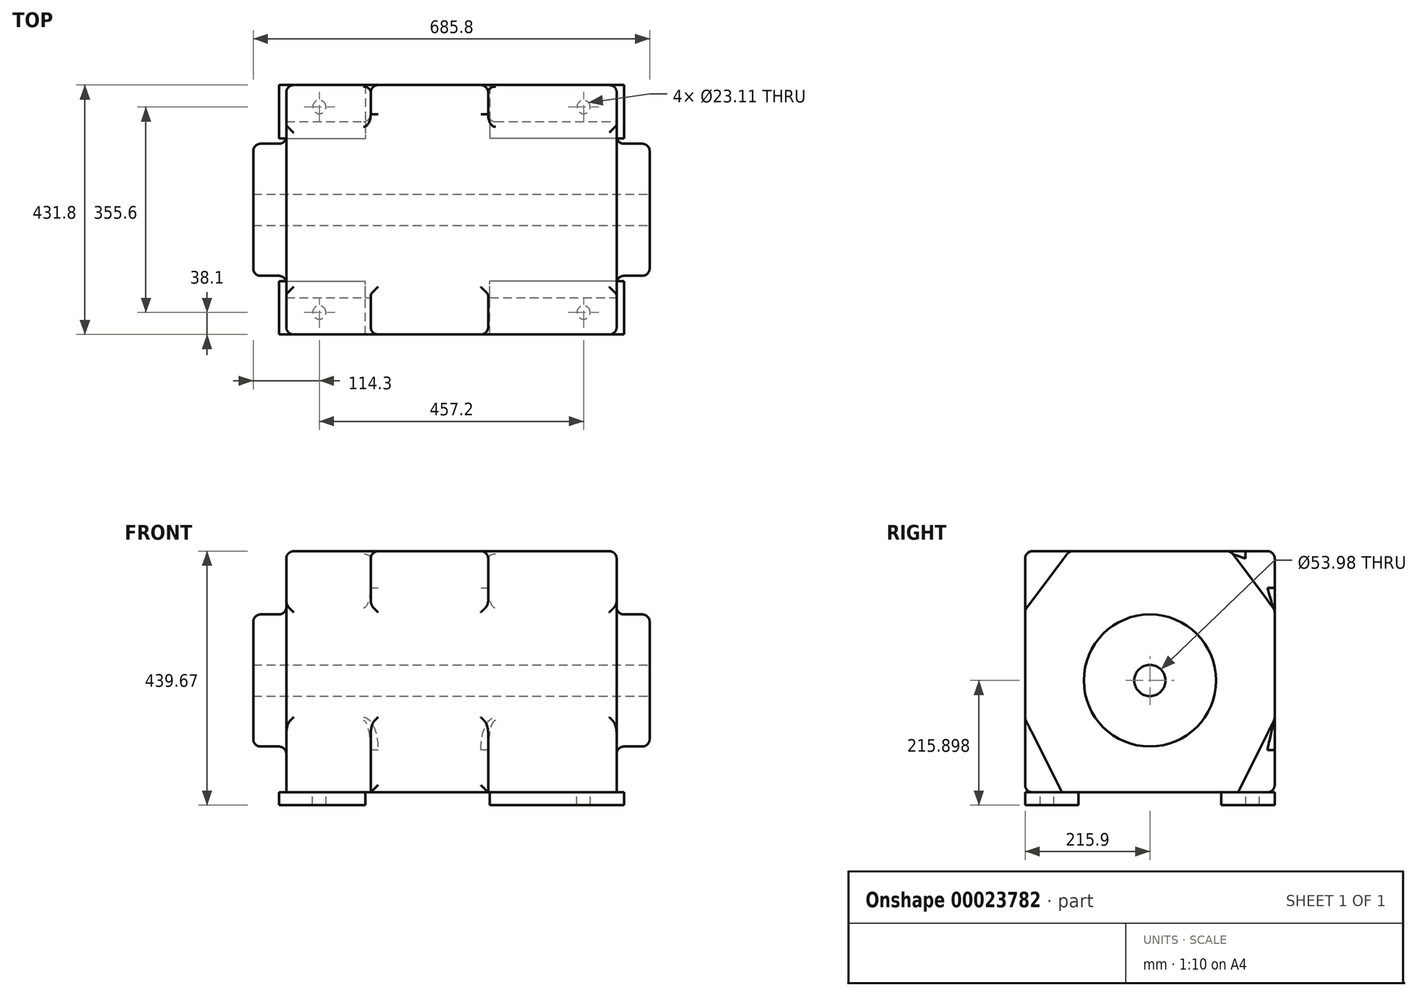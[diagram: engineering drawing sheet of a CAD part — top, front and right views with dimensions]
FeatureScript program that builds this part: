
annotation { "Feature Type Name" : "Feature", "Feature Type Description" : "" }
export const myFeature = defineFeature(function(context is Context, id is Id, definition is map)
    precondition{}
    {
        {
            var Q0;
            Q0=qCreatedBy(makeId("Top.planeOp"),FACE);
            var sketch = newSketch(context, id + "F0", { "sketchPlane" : qUnion([Q0])});
            skLineSegment(sketch, "E0", {"start": v(0, 97.33) * mm, "end": v(0, -215.9) * mm, "construction": true});
            skLineSegment(sketch, "E1", {"start": v(-109.5, 0) * mm, "end": v(101.39, 0) * mm, "construction": true});
            skLineSegment(sketch, "E2.0", {"start": v(-298.45, 215.9) * mm, "end": v(-298.45, -215.9) * mm, "construction": true});
            skLineSegment(sketch, "E3.0", {"start": v(-298.45, -215.9) * mm, "end": v(298.45, -215.9) * mm, "construction": true});
            skLineSegment(sketch, "E4.MirrorCS", {"start": v(298.45, 215.9) * mm, "end": v(298.45, -215.9) * mm, "construction": true});
            skLineSegment(sketch, "E5.MirrorCS", {"start": v(-298.45, 215.9) * mm, "end": v(298.45, 215.9) * mm, "construction": true});
            skPoint(sketch, "E6.orphan", {"position": v(-298.45, 97.33) * mm});
            skPoint(sketch, "E7.orphan", {"position": v(298.45, 97.33) * mm});
            skLineSegment(sketch, "E8.bottom", {"start": v(-298.45, -215.9) * mm, "end": v(-149.1, -215.9) * mm});
            skLineSegment(sketch, "E8.top", {"start": v(-298.45, -123.7) * mm, "end": v(-149.1, -123.7) * mm});
            skLineSegment(sketch, "E8.left", {"start": v(-298.45, -215.9) * mm, "end": v(-298.45, -123.7) * mm});
            skLineSegment(sketch, "E8.right", {"start": v(-149.1, -215.9) * mm, "end": v(-149.1, -123.7) * mm});
            skLineSegment(sketch, "E9.bottom", {"start": v(298.45, -215.9) * mm, "end": v(66.55, -215.9) * mm});
            skLineSegment(sketch, "E9.top", {"start": v(298.45, -123.7) * mm, "end": v(66.55, -123.7) * mm});
            skLineSegment(sketch, "E9.left", {"start": v(298.45, -215.9) * mm, "end": v(298.45, -123.7) * mm});
            skLineSegment(sketch, "E9.right", {"start": v(66.55, -215.9) * mm, "end": v(66.55, -123.7) * mm});
            skLineSegment(sketch, "E10.0", {"start": v(-228.6, 97.33) * mm, "end": v(-228.6, -215.9) * mm, "construction": true});
            skLineSegment(sketch, "E11.0", {"start": v(-228.6, -177.8) * mm, "end": v(101.39, -177.8) * mm, "construction": true});
            skCircle(sketch, "E12", {"center": v(-228.6, -177.8) * mm, "radius": 11.56 * mm});
            skCircle(sketch, "E13.MirrorC", {"center": v(228.6, -177.8) * mm, "radius": 11.56 * mm});
            skCircle(sketch, "E14.MirrorC", {"center": v(-228.6, 177.8) * mm, "radius": 11.56 * mm});
            skLineSegment(sketch, "E15.MirrorCS", {"start": v(-298.45, 123.7) * mm, "end": v(-149.1, 123.7) * mm});
            skLineSegment(sketch, "E16.MirrorCS", {"start": v(-298.45, 215.9) * mm, "end": v(-149.1, 215.9) * mm});
            skLineSegment(sketch, "E17.MirrorCS", {"start": v(-298.45, 215.9) * mm, "end": v(-298.45, 123.7) * mm});
            skLineSegment(sketch, "E18.MirrorCS", {"start": v(-149.1, 215.9) * mm, "end": v(-149.1, 123.7) * mm});
            skLineSegment(sketch, "E19.MirrorCS", {"start": v(298.45, 215.9) * mm, "end": v(298.45, 123.7) * mm});
            skLineSegment(sketch, "E20.MirrorCS", {"start": v(-228.6, 177.8) * mm, "end": v(101.39, 177.8) * mm, "construction": true});
            skLineSegment(sketch, "E21.MirrorCS", {"start": v(-298.45, 215.9) * mm, "end": v(298.45, 215.9) * mm});
            skLineSegment(sketch, "E22.MirrorCS", {"start": v(298.45, 123.7) * mm, "end": v(66.55, 123.7) * mm});
            skCircle(sketch, "E23.MirrorC", {"center": v(228.6, 177.8) * mm, "radius": 11.56 * mm});
            skLineSegment(sketch, "E24.MirrorCS", {"start": v(298.45, 215.9) * mm, "end": v(66.55, 215.9) * mm});
            skLineSegment(sketch, "E25.MirrorCS", {"start": v(66.55, 215.9) * mm, "end": v(66.55, 123.7) * mm});
            skSolve(sketch);
        }
        {
            var Q0;
            Q0 = qSketchRegion(id + "F0", true);
            extrude(context, id + "F1", {"entities" : qUnion([Q0]), "oppositeDirection" : true, "depth" : 22.35 * mm});
        }
        {
            var Q0;
            Q0=makeQuery(id+"F1.opExtrude","CAP_FACE",FACE,{"disambiguationData":[OSD([sQuery(id+"F0.wireOp",EDGE,"E14.MirrorC"),sQuery(id+"F0.wireOp",EDGE,"E15.MirrorCS"),sQuery(id+"F0.wireOp",EDGE,"E17.MirrorCS"),sQuery(id+"F0.wireOp",EDGE,"E18.MirrorCS"),sQuery(id+"F0.wireOp",EDGE,"E21.MirrorCS")])],"isStart":true});
            var sketch = newSketch(context, id + "F2", { "sketchPlane" : qUnion([Q0])});
            skLineSegment(sketch, "E26.bottom", {"start": v(-285.75, 139.7) * mm, "end": v(285.75, 139.7) * mm});
            skLineSegment(sketch, "E26.top", {"start": v(-285.75, -139.7) * mm, "end": v(285.75, -139.7) * mm});
            skLineSegment(sketch, "E26.left", {"start": v(-285.75, 139.7) * mm, "end": v(-285.75, -139.7) * mm});
            skLineSegment(sketch, "E26.right", {"start": v(285.75, 139.7) * mm, "end": v(285.75, -139.7) * mm});
            skSolve(sketch);
        }
        {
            var Q0;
            Q0 = qSketchRegion(id + "F2", true);
            extrude(context, id + "F3", {"entities" : qUnion([Q0]), "operationType" : NewBodyOperationType.ADD, "depth" : 417.32 * mm});
        }
        {
            var Q0;
            Q0=makeQuery(id+"F3.opExtrude","SWEPT_FACE",FACE,{"disambiguationData":[OSD([sQuery(id+"F2.wireOp",EDGE,"E26.right")])]});
            var sketch = newSketch(context, id + "F4", { "sketchPlane" : qUnion([Q0])});
            skLineSegment(sketch, "E27.0", {"start": v(-215.9, 0) * mm, "end": v(-123.7, 0) * mm, "construction": true});
            skLineSegment(sketch, "E28.0", {"start": v(215.9, 0) * mm, "end": v(123.7, 0) * mm, "construction": true});
            skLineSegment(sketch, "E29.0", {"start": v(139.7, 417.32) * mm, "end": v(-139.7, 417.32) * mm, "construction": true});
            skLineSegment(sketch, "E30", {"start": v(215.9, 0) * mm, "end": v(215.9, 417.32) * mm, "construction": true});
            skLineSegment(sketch, "E31.bottom", {"start": v(0, 0) * mm, "end": v(215.9, 0) * mm});
            skLineSegment(sketch, "E31.top", {"start": v(0, 417.32) * mm, "end": v(139.7, 417.32) * mm});
            skLineSegment(sketch, "E31.left", {"start": v(0, 0) * mm, "end": v(0, 417.32) * mm});
            skLineSegment(sketch, "E31.right", {"start": v(215.9, 127) * mm, "end": v(215.9, 315.72) * mm});
            skLineSegment(sketch, "E32", {"start": v(152.4, 0) * mm, "end": v(215.9, 127) * mm});
            skLineSegment(sketch, "E33", {"start": v(139.7, 417.32) * mm, "end": v(215.9, 315.72) * mm});
            skLineSegment(sketch, "E34.MirrorCS", {"start": v(-215.9, 0) * mm, "end": v(-123.7, 0) * mm});
            skLineSegment(sketch, "E35.MirrorCS", {"start": v(-152.4, 0) * mm, "end": v(-215.9, 127) * mm});
            skLineSegment(sketch, "E36.MirrorCS", {"start": v(0, 417.32) * mm, "end": v(-139.7, 417.32) * mm});
            skLineSegment(sketch, "E37.MirrorCS", {"start": v(0, 0) * mm, "end": v(-215.9, 0) * mm});
            skLineSegment(sketch, "E38.MirrorCS", {"start": v(-215.9, 127) * mm, "end": v(-215.9, 315.72) * mm});
            skLineSegment(sketch, "E39.MirrorCS", {"start": v(-215.9, 127) * mm, "end": v(-215.9, 417.32) * mm});
            skLineSegment(sketch, "E40.MirrorCS", {"start": v(-139.7, 417.32) * mm, "end": v(-215.9, 315.72) * mm});
            skSolve(sketch);
        }
        {
            var Q0;
            Q0 = qSketchRegion(id + "F4", true);
            var Q1;
            Q1=makeQuery(id+"F3.opExtrude","SWEPT_FACE",FACE,{"disambiguationData":[OSD([sQuery(id+"F2.wireOp",EDGE,"E26.left")])]});
            extrude(context, id + "F5", {"entities" : qUnion([Q0]), "operationType" : NewBodyOperationType.ADD, "endBound" : BoundingType.UP_TO_SURFACE, "oppositeDirection" : true, "endBoundEntityFace" : qUnion([Q1]), "depth" : 25.4 * mm});
        }
        {
            var Q0;
            Q0=qCreatedBy(makeId("Right.planeOp"),FACE);
            var sketch = newSketch(context, id + "F6", { "sketchPlane" : qUnion([Q0])});
            skLineSegment(sketch, "E41.0", {"start": v(-215.9, 0) * mm, "end": v(-123.7, 0) * mm, "construction": true});
            skLineSegment(sketch, "E42.0", {"start": v(215.9, 0) * mm, "end": v(123.7, 0) * mm, "construction": true});
            skLineSegment(sketch, "E43.bottom", {"start": v(215.9, 0) * mm, "end": v(-215.9, 0) * mm, "construction": true});
            skLineSegment(sketch, "E43.top", {"start": v(215.9, 0) * mm, "end": v(-215.9, 0) * mm, "construction": true});
            skLineSegment(sketch, "E43.left", {"start": v(215.9, 0) * mm, "end": v(215.9, 0) * mm});
            skLineSegment(sketch, "E43.right", {"start": v(-215.9, 0) * mm, "end": v(-215.9, 0) * mm});
            skLineSegment(sketch, "E44.0", {"start": v(139.7, 417.32) * mm, "end": v(-139.7, 417.32) * mm, "construction": true});
            skLineSegment(sketch, "E45", {"start": v(215.9, 0) * mm, "end": v(215.9, 417.32) * mm, "construction": true});
            skLineSegment(sketch, "E46.bottom", {"start": v(215.9, 417.32) * mm, "end": v(-215.9, 417.32) * mm});
            skLineSegment(sketch, "E46.top", {"start": v(215.9, 0) * mm, "end": v(-215.9, 0) * mm});
            skLineSegment(sketch, "E46.left", {"start": v(215.9, 417.32) * mm, "end": v(215.9, 0) * mm});
            skLineSegment(sketch, "E46.right", {"start": v(-215.9, 417.32) * mm, "end": v(-215.9, 0) * mm});
            skSolve(sketch);
        }
        {
            var Q0;
            Q0=makeQuery(id+"F6.imprint","IMPRINT",FACE,{"disambiguationData":[TD([[makeQuery(id+"F6.imprint","IMPRINT",EDGE,{"derivedFrom":sQuery(id+"F6.wireOp",EDGE,"E46.bottom")}),1.0]])]});
            var sketch = newSketch(context, id + "F7", { "sketchPlane" : qUnion([Q0])});
            skSolve(sketch);
        }
        {
            var Q0;
            Q0 = qSketchRegion(id + "F7", true);
            var Q1;
            Q1=makeQuery(id+"F6.imprint","IMPRINT",FACE,{"disambiguationData":[TD([[makeQuery(id+"F6.imprint","IMPRINT",EDGE,{"derivedFrom":sQuery(id+"F6.wireOp",EDGE,"E46.bottom")}),1.0]])]});
            var Q2;
            Q2=makeQuery(id+"F1.opExtrude","SWEPT_FACE",FACE,{"disambiguationData":[OSD([sQuery(id+"F0.wireOp",EDGE,"E18.MirrorCS")])]});
            extrude(context, id + "F8", {"entities" : qUnion([Q0, Q1]), "operationType" : NewBodyOperationType.ADD, "oppositeDirection" : true, "endBoundEntityFace" : qUnion([Q2]), "depth" : 139.7 * mm, "hasSecondDirection" : true, "secondDirectionOppositeDirection" : false, "secondDirectionDepth" : 63.5 * mm});
        }
        {
            var Q0;
            Q0=makeQuery(id+"F8.boolean.opBoolean","MERGE",FACE,{"derivedFrom":[makeQuery(id+"F5.opExtrude","SWEPT_FACE",FACE,{"disambiguationData":[OSD([sQuery(id+"F4.wireOp",EDGE,"E31.right")])]}),makeQuery(id+"F8.opExtrude","SWEPT_FACE",FACE,{"disambiguationData":[OSD([sQuery(id+"F6.wireOp",EDGE,"E46.left")])]})]});
            var Q1;
            Q1=makeQuery(id+"F8.boolean.opBoolean","INTERSECT",EDGE,{"derivedFrom":[makeQuery(id+"F5.opExtrude","SWEPT_FACE",FACE,{"disambiguationData":[OSD([sQuery(id+"F4.wireOp",EDGE,"E32")])]}),makeQuery(id+"F8.opExtrude","CAP_FACE",FACE,{"disambiguationData":[OSD([sQuery(id+"F6.wireOp",EDGE,"E46.bottom"),sQuery(id+"F6.wireOp",EDGE,"E46.top"),sQuery(id+"F6.wireOp",EDGE,"E46.left"),sQuery(id+"F6.wireOp",EDGE,"E46.right")])],"isStart":true})]});
            var Q2;
            Q2=makeQuery(id+"F8.boolean.opBoolean","INTERSECT",EDGE,{"derivedFrom":[makeQuery(id+"F5.opExtrude","SWEPT_FACE",FACE,{"disambiguationData":[OSD([sQuery(id+"F4.wireOp",EDGE,"E33")])]}),makeQuery(id+"F8.opExtrude","CAP_FACE",FACE,{"disambiguationData":[OSD([sQuery(id+"F6.wireOp",EDGE,"E46.bottom"),sQuery(id+"F6.wireOp",EDGE,"E46.top"),sQuery(id+"F6.wireOp",EDGE,"E46.left"),sQuery(id+"F6.wireOp",EDGE,"E46.right")])],"isStart":true})]});
            var Q3;
            Q3=makeQuery(id+"F8.boolean.opBoolean","INTERSECT",EDGE,{"derivedFrom":[makeQuery(id+"F5.opExtrude","SWEPT_FACE",FACE,{"disambiguationData":[OSD([sQuery(id+"F4.wireOp",EDGE,"E32")])]}),makeQuery(id+"F8.opExtrude","CAP_FACE",FACE,{"disambiguationData":[OSD([sQuery(id+"F6.wireOp",EDGE,"E46.bottom"),sQuery(id+"F6.wireOp",EDGE,"E46.top"),sQuery(id+"F6.wireOp",EDGE,"E46.left"),sQuery(id+"F6.wireOp",EDGE,"E46.right")])],"isStart":false})]});
            var Q4;
            Q4=makeQuery(id+"F8.boolean.opBoolean","INTERSECT",EDGE,{"derivedFrom":[makeQuery(id+"F5.opExtrude","SWEPT_FACE",FACE,{"disambiguationData":[OSD([sQuery(id+"F4.wireOp",EDGE,"E33")])]}),makeQuery(id+"F8.opExtrude","CAP_FACE",FACE,{"disambiguationData":[OSD([sQuery(id+"F6.wireOp",EDGE,"E46.bottom"),sQuery(id+"F6.wireOp",EDGE,"E46.top"),sQuery(id+"F6.wireOp",EDGE,"E46.left"),sQuery(id+"F6.wireOp",EDGE,"E46.right")])],"isStart":false})]});
            var Q5;
            Q5=makeQuery(id+"F8.boolean.opBoolean","MERGE",FACE,{"derivedFrom":[makeQuery(id+"F5.opExtrude","SWEPT_FACE",FACE,{"disambiguationData":[OSD([sQuery(id+"F4.wireOp",EDGE,"E39.MirrorCS")])]}),makeQuery(id+"F8.opExtrude","SWEPT_FACE",FACE,{"disambiguationData":[OSD([sQuery(id+"F6.wireOp",EDGE,"E46.right")])]})]});
            fillet(context, id + "F9", {"entities" : qUnion([Q0, Q1, Q2, Q3, Q4, Q5]), "radius" : 12.7 * mm, "tangentPropagation" : true, "allowEdgeOverflow" : false});
        }
        {
            var Q0;
            Q0=makeQuery(id+"F8.boolean.opBoolean","MERGE",FACE,{"derivedFrom":[makeQuery(id+"F3.opExtrude","CAP_FACE",FACE,{"disambiguationData":[OSD([sQuery(id+"F2.wireOp",EDGE,"E26.bottom"),sQuery(id+"F2.wireOp",EDGE,"E26.top"),sQuery(id+"F2.wireOp",EDGE,"E26.left"),sQuery(id+"F2.wireOp",EDGE,"E26.right")])],"isStart":false}),makeQuery(id+"F8.opExtrude","SWEPT_FACE",FACE,{"disambiguationData":[OSD([sQuery(id+"F6.wireOp",EDGE,"E46.bottom")])]})]});
            fillet(context, id + "F10", {"entities" : qUnion([Q0]), "radius" : 12.7 * mm, "tangentPropagation" : true, "allowEdgeOverflow" : false});
        }
        {
            var Q0;
            Q0=makeQuery(id+"F7.imprint","IMPRINT",FACE,{"disambiguationData":[TD([[makeQuery(id+"F7.imprint","IMPRINT",EDGE,{"derivedFrom":makeQuery(id+"F6.imprint","IMPRINT",EDGE,{"derivedFrom":sQuery(id+"F6.wireOp",EDGE,"E46.bottom")})}),1.0]])]});
            var sketch = newSketch(context, id + "F11", { "sketchPlane" : qUnion([Q0])});
            skLineSegment(sketch, "E47.0", {"start": v(-215.9, -22.35) * mm, "end": v(-123.7, -22.35) * mm, "construction": true});
            skLineSegment(sketch, "E48.0", {"start": v(-215.9, 193.55) * mm, "end": v(0, 193.55) * mm, "construction": true});
            skLineSegment(sketch, "E49", {"start": v(0, 0) * mm, "end": v(0, 468.14) * mm, "construction": true});
            skCircle(sketch, "E50", {"center": v(0, 193.55) * mm, "radius": 114.3 * mm});
            skSolve(sketch);
        }
        {
            var Q0;
            Q0 = qSketchRegion(id + "F11", true);
            extrude(context, id + "F12", {"entities" : qUnion([Q0]), "operationType" : NewBodyOperationType.ADD, "depth" : 342.9 * mm, "hasSecondDirection" : true, "secondDirectionOppositeDirection" : true, "secondDirectionDepth" : 342.9 * mm});
        }
        {
            var Q0;
            Q0=makeQuery(id+"F12.boolean.opBoolean","INTERSECT",EDGE,{"derivedFrom":[makeQuery(id+"F5.boolean.opBoolean","MERGE",FACE,{"derivedFrom":[makeQuery(id+"F3.opExtrude","SWEPT_FACE",FACE,{"disambiguationData":[OSD([sQuery(id+"F2.wireOp",EDGE,"E26.right")])]}),makeQuery(id+"F5.opExtrude","CAP_FACE",FACE,{"disambiguationData":[OSD([sQuery(id+"F4.wireOp",EDGE,"E31.bottom"),sQuery(id+"F4.wireOp",EDGE,"E31.top"),sQuery(id+"F4.wireOp",EDGE,"E31.right"),sQuery(id+"F4.wireOp",EDGE,"E32"),sQuery(id+"F4.wireOp",EDGE,"E33"),sQuery(id+"F4.wireOp",EDGE,"E35.MirrorCS"),sQuery(id+"F4.wireOp",EDGE,"E36.MirrorCS"),sQuery(id+"F4.wireOp",EDGE,"E37.MirrorCS"),sQuery(id+"F4.wireOp",EDGE,"E39.MirrorCS"),sQuery(id+"F4.wireOp",EDGE,"E40.MirrorCS")])],"isStart":true})]}),makeQuery(id+"F12.opExtrude","SWEPT_FACE",FACE,{"disambiguationData":[OSD([sQuery(id+"F11.wireOp",EDGE,"E50")])]})]});
            var Q1;
            Q1=makeQuery(id+"F12.opExtrude","CAP_EDGE",EDGE,{"disambiguationData":[OSD([sQuery(id+"F11.wireOp",EDGE,"E50")])],"isStart":false});
            var Q2;
            Q2=makeQuery(id+"F12.opExtrude","CAP_FACE",FACE,{"disambiguationData":[OSD([sQuery(id+"F11.wireOp",EDGE,"E50")])],"isStart":true});
            var Q3;
            Q3=makeQuery(id+"F12.boolean.opBoolean","INTERSECT",EDGE,{"derivedFrom":[makeQuery(id+"F5.boolean.opBoolean","MERGE",FACE,{"derivedFrom":[makeQuery(id+"F3.opExtrude","SWEPT_FACE",FACE,{"disambiguationData":[OSD([sQuery(id+"F2.wireOp",EDGE,"E26.left")])]}),makeQuery(id+"F5.opExtrude","CAP_FACE",FACE,{"disambiguationData":[OSD([sQuery(id+"F4.wireOp",EDGE,"E31.bottom"),sQuery(id+"F4.wireOp",EDGE,"E31.top"),sQuery(id+"F4.wireOp",EDGE,"E31.right"),sQuery(id+"F4.wireOp",EDGE,"E32"),sQuery(id+"F4.wireOp",EDGE,"E33"),sQuery(id+"F4.wireOp",EDGE,"E35.MirrorCS"),sQuery(id+"F4.wireOp",EDGE,"E36.MirrorCS"),sQuery(id+"F4.wireOp",EDGE,"E37.MirrorCS"),sQuery(id+"F4.wireOp",EDGE,"E39.MirrorCS"),sQuery(id+"F4.wireOp",EDGE,"E40.MirrorCS")])],"isStart":false})]}),makeQuery(id+"F12.opExtrude","SWEPT_FACE",FACE,{"disambiguationData":[OSD([sQuery(id+"F11.wireOp",EDGE,"E50")])]})]});
            fillet(context, id + "F13", {"entities" : qUnion([Q0, Q1, Q2, Q3]), "radius" : 12.7 * mm, "tangentPropagation" : true, "allowEdgeOverflow" : false});
        }
        {
            var Q0;
            Q0=makeQuery(id+"F12.opExtrude","CAP_FACE",FACE,{"disambiguationData":[OSD([sQuery(id+"F11.wireOp",EDGE,"E50")])],"isStart":false});
            var sketch = newSketch(context, id + "F14", { "sketchPlane" : qUnion([Q0])});
            skCircle(sketch, "E51.0.0", {"center": v(0, 193.55) * mm, "radius": 101.6 * mm, "construction": true});
            skCircle(sketch, "E52", {"center": v(0, 193.55) * mm, "radius": 26.99 * mm});
            skSolve(sketch);
        }
        {
            var Q0;
            Q0 = qSketchRegion(id + "F14", true);
            extrude(context, id + "F15", {"entities" : qUnion([Q0]), "operationType" : NewBodyOperationType.REMOVE, "endBound" : BoundingType.THROUGH_ALL, "oppositeDirection" : true, "depth" : 25.4 * mm});
        }
    });
